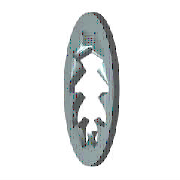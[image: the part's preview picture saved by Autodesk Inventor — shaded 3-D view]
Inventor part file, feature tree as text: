
AUTODESK INVENTOR PART (.ipt)
format: ipt  version: 2021 (Build 250183000, 183)  size: 174,592 bytes
history: native  units: mm (DEFAULTED — no unit token found)
features: sketch x2, extrude x1, pattern_circular x1, other x1, plane x1
ambient origin geometry x7: Origin, YZ Plane, XY Plane, X Axis, Y Axis, Z Axis, Center Point
bodies: Solid1 (feature_tree), Body (feature_tree)
feature tree (6):
  extrude  "Cut"  Depth=6.0mm
  pattern_circular  "Cuts"  [2 undecoded]
  other  "Work Axis2"
  plane  "Work Plane1"
  sketch  "Sketch1"  dims[d0=3.2mm d1=6.0mm]
  sketch  "Sketch2"  dims[d2=0.4mm d3=0.0mm d6=4.6mm d7=2.243995mm d8=0.4mm d9=0.0mm d10=0.096mm d11=70.0mm d13=360.0deg d14=0.0mm d15=0.0mm d20=0.0mm d21=0.0mm]
note: 2 required parameter values undecoded (feature->parameter linkage not recoverable at this tier; creation-order binding heuristic only, values carry confidence <= 0.55)
